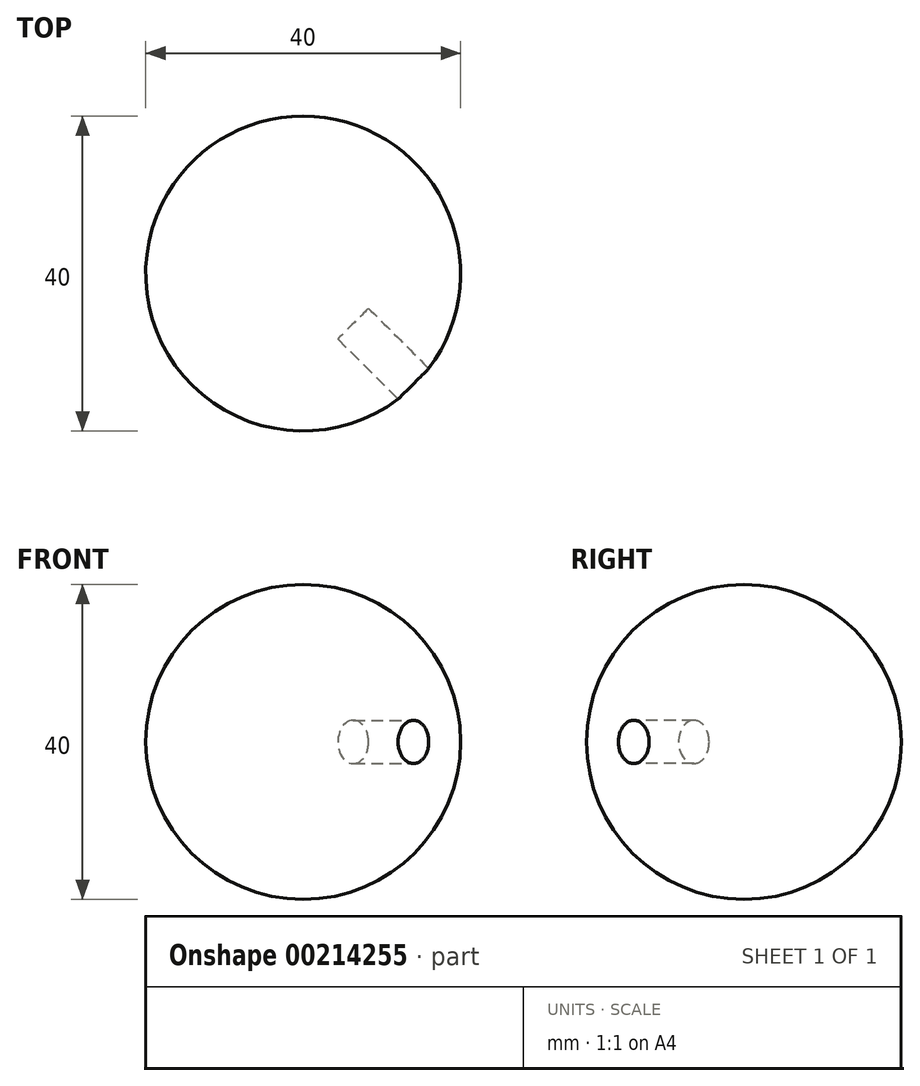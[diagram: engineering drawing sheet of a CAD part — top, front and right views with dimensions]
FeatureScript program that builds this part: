
annotation { "Feature Type Name" : "Feature", "Feature Type Description" : "" }
export const myFeature = defineFeature(function(context is Context, id is Id, definition is map)
    precondition{}
    {
        {
            assignVariable(context, id + "F0", {"name" : "d", "anyValue" : 5.5});
        }
        {
            var Q0;
            Q0=qCreatedBy(makeId("Front.planeOp"),FACE);
            var sketch = newSketch(context, id + "F1", { "sketchPlane" : qUnion([Q0])});
            skArc(sketch, "E0", {"start": v(0, -20) * mm, "mid": v(-20, 0) * mm, "end": v(0, 20) * mm});
            skLineSegment(sketch, "E1", {"start": v(0, 20) * mm, "end": v(0, -20) * mm});
            skSolve(sketch);
        }
        {
            var Q0;
            Q0=qSketchRegion(id+"F1",true);
            var Q1;
            Q1=sQuery(id+"F1.wireOp",EDGE,"E1");
            revolve(context, id + "F2", {"entities" : qUnion([Q0]), "axis" : qUnion([Q1]), "revolveType" : RevolveType.FULL});
        }
        {
            var Q0;
            Q0=qCreatedBy(makeId("Top.planeOp"),FACE);
            var sketch = newSketch(context, id + "F3", { "sketchPlane" : qUnion([Q0])});
            skCircle(sketch, "E2.cCircle", {"center": v(0, 0) * mm, "radius": 10 * mm, "construction": true});
            skLineSegment(sketch, "E2.0", {"start": v(-19.32, -5.18) * mm, "end": v(5.18, 19.32) * mm});
            skLineSegment(sketch, "E2.1", {"start": v(5.18, 19.32) * mm, "end": v(14.14, -14.14) * mm});
            skLineSegment(sketch, "E2.2", {"start": v(14.14, -14.14) * mm, "end": v(-19.32, -5.18) * mm});
            skPoint(sketch, "E2.0.midPoint", {"position": v(-7.07, 7.07) * mm});
            skLineSegment(sketch, "E3", {"start": v(0, 0) * mm, "end": v(14.14, -14.14) * mm, "construction": true});
            skLineSegment(sketch, "E4", {"start": v(0, 0) * mm, "end": v(0, -22.23) * mm, "construction": true});
            skSolve(sketch);
        }
        {
            var Q0;
            Q0=sQuery(id+"F3.wireOp",VERTEX,"E2.2.start");
            var Q1;
            Q1=sQuery(id+"F3.wireOp",EDGE,"E3");
            cPlane(context, id + "F4", {"entities" : qUnion([Q0, Q1]), "cplaneType" : CPlaneType.LINE_POINT, "offset" : 25 * mm, "width" : 150 * mm, "height" : 150 * mm});
        }
        {
            var Q0;
            Q0=qCreatedBy(id+"F4.planeOp",FACE);
            var sketch = newSketch(context, id + "F5", { "sketchPlane" : qUnion([Q0])});
            skCircle(sketch, "E5", {"center": v(0, 0) * mm, "radius": 2.75 * mm});
            skSolve(sketch);
        }
        {
            var Q0;
            Q0 = qSketchRegion(id + "F5", true);
            extrude(context, id + "F6", {"entities" : qUnion([Q0]), "operationType" : NewBodyOperationType.REMOVE, "oppositeDirection" : true, "depth" : (getVariable(context, 'd') * 2) * mm});
        }
    });
